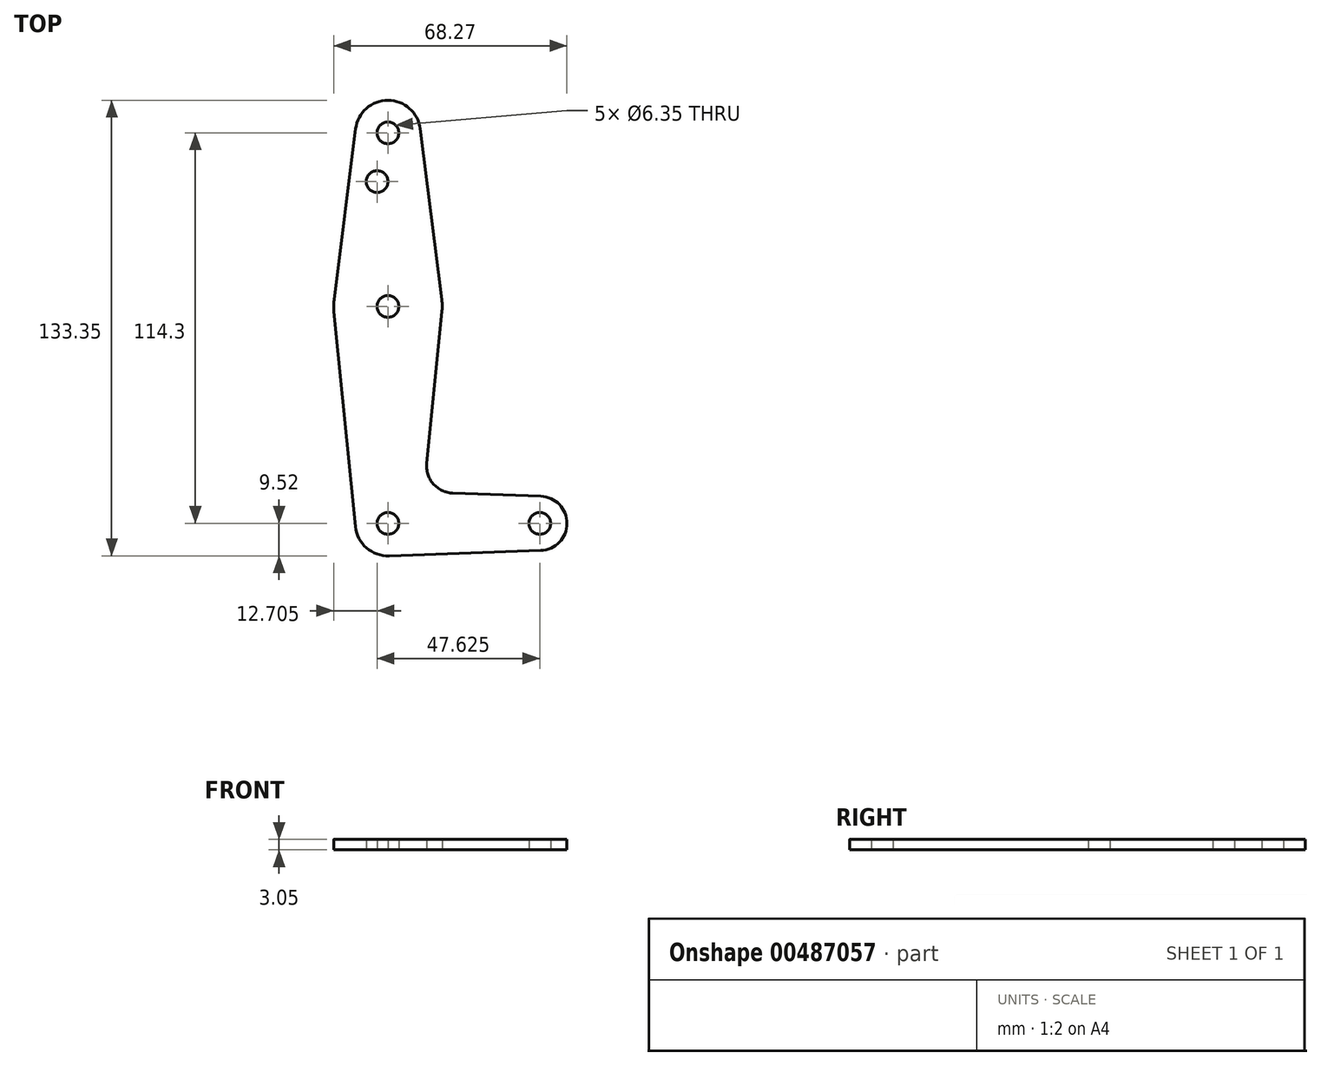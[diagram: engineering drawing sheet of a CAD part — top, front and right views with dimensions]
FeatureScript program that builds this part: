
annotation { "Feature Type Name" : "Feature", "Feature Type Description" : "" }
export const myFeature = defineFeature(function(context is Context, id is Id, definition is map)
    precondition{}
    {
        {
            var Q0;
            Q0=qCreatedBy(makeId("Top.planeOp"),FACE);
            var sketch = newSketch(context, id + "F0", { "sketchPlane" : qUnion([Q0])});
            skLineSegment(sketch, "E0", {"start": v(0, 0) * mm, "end": v(0, 114.3) * mm, "construction": true});
            skLineSegment(sketch, "E1", {"start": v(0, 0) * mm, "end": v(44.45, 0) * mm, "construction": true});
            skCircle(sketch, "E2", {"center": v(0, 114.3) * mm, "radius": 9.53 * mm});
            skCircle(sketch, "E3", {"center": v(0, 0) * mm, "radius": 9.53 * mm});
            skCircle(sketch, "E4", {"center": v(0, 63.5) * mm, "radius": 15.88 * mm});
            skCircle(sketch, "E5", {"center": v(44.45, 0) * mm, "radius": 7.94 * mm});
            skLineSegment(sketch, "E6", {"start": v(9.45, 115.5) * mm, "end": v(15.75, 65.48) * mm});
            skLineSegment(sketch, "E7", {"start": v(-9.45, 115.5) * mm, "end": v(-15.75, 65.48) * mm});
            skLineSegment(sketch, "E8", {"start": v(15.8, 61.91) * mm, "end": v(11.34, 17.6) * mm});
            skLineSegment(sketch, "E9", {"start": v(-15.8, 61.91) * mm, "end": v(-9.48, -0.95) * mm});
            skLineSegment(sketch, "E10", {"start": v(18.97, 8.85) * mm, "end": v(44.73, 7.93) * mm});
            skLineSegment(sketch, "E11", {"start": v(0.34, -9.52) * mm, "end": v(44.73, -7.93) * mm});
            skCircle(sketch, "E12", {"center": v(0, 114.3) * mm, "radius": 3.18 * mm});
            skCircle(sketch, "E13", {"center": v(-3.18, 100.03) * mm, "radius": 3.18 * mm});
            skCircle(sketch, "E14", {"center": v(0, 63.5) * mm, "radius": 3.18 * mm});
            skCircle(sketch, "E15", {"center": v(0, 0) * mm, "radius": 3.18 * mm});
            skCircle(sketch, "E16", {"center": v(44.45, 0) * mm, "radius": 3.18 * mm});
            skArc(sketch, "E17.filletArc", {"start": v(11.34, 17.6) * mm, "mid": v(13.26, 11.57) * mm, "end": v(18.97, 8.85) * mm});
            skSolve(sketch);
        }
        {
            var Q0;
            Q0=makeQuery(id+"F0.imprint","IMPRINT",FACE,{"disambiguationData":[TD([[makeQuery(id+"F0.imprint","IMPRINT",EDGE,{"derivedFrom":sQuery(id+"F0.wireOp",EDGE,"E12")}),-1.0]])]});
            var Q1;
            {var subQ0=sQuery(id+"F0.wireOp",EDGE,"E6");Q1=makeQuery(id+"F0.imprint","IMPRINT",FACE,{"disambiguationData":[TD([[makeQuery(id+"F0.imprint","IMPRINT",EDGE,{"derivedFrom":subQ0}),-1.0]])]});}
            var Q2;
            Q2=makeQuery(id+"F0.imprint","IMPRINT",FACE,{"disambiguationData":[TD([[makeQuery(id+"F0.imprint","IMPRINT",EDGE,{"derivedFrom":sQuery(id+"F0.wireOp",EDGE,"E14")}),-1.0]])]});
            var Q3;
            {var subQ0=sQuery(id+"F0.wireOp",EDGE,"E8");Q3=makeQuery(id+"F0.imprint","IMPRINT",FACE,{"disambiguationData":[TD([[makeQuery(id+"F0.imprint","IMPRINT",EDGE,{"derivedFrom":subQ0}),-1.0]])]});}
            var Q4;
            Q4=makeQuery(id+"F0.imprint","IMPRINT",FACE,{"disambiguationData":[TD([[makeQuery(id+"F0.imprint","IMPRINT",EDGE,{"derivedFrom":sQuery(id+"F0.wireOp",EDGE,"E15")}),-1.0]])]});
            var Q5;
            Q5=makeQuery(id+"F0.imprint","IMPRINT",FACE,{"disambiguationData":[TD([[makeQuery(id+"F0.imprint","IMPRINT",EDGE,{"derivedFrom":sQuery(id+"F0.wireOp",EDGE,"E16")}),-1.0]])]});
            extrude(context, id + "F1", {"entities" : qUnion([Q0, Q1, Q2, Q3, Q4, Q5]), "depth" : 3.05 * mm});
        }
    });
